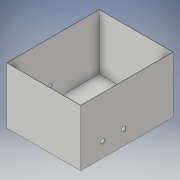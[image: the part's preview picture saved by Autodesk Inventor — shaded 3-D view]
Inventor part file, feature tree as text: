
AUTODESK INVENTOR PART (.ipt)
format: ipt  version: 2018 (Build 220112000, 112)  size: 176,640 bytes
history: native  units: in
note: dims shown in document units (in); Inventor stores cm internally (conversion verified against a paired STEP export)
features: extrude x7, sketch x7
ambient origin geometry x8: Origin, YZ Plane, XZ Plane, XY Plane, X Axis, Y Axis, Z Axis, Center Point
bodies: Solid1 (feature_tree)
feature tree (14):
  extrude  "Extrusion1"  Depth=5.0in
  extrude  "Extrusion2"  Depth=3.96in
  extrude  "Extrusion3"  Depth=3.0in TaperAngle=0.0deg
  extrude  "Extrusion4"  Depth=2.0in
  extrude  "Extrusion5"  Depth=0.164in
  extrude  "Extrusion6"  Depth=1.929in
  extrude  "Extrusion7"  Depth=1.722in
  sketch  "Sketch1"  dims[d0=4.0in d1=5.0in]
  sketch  "Sketch2"  dims[d2=0.04in d3=0.0in d4=3.96in]
  sketch  "Sketch3"  dims[d5=4.96in d6=3.0in d7=0.0in]
  sketch  "Sketch4"  dims[d8=1.0in d9=2.0in]
  sketch  "Sketch5"  dims[d10=0.164in d11=0.164in]
  sketch  "Sketch6"  dims[d12=0.0in d13=0.0in d14=1.929in]
  sketch  "Sketch7"  dims[d15=3.504in d16=1.722in d17=3.504in d18=2.717in d27=0.112in d28=0.112in d29=0.112in d30=0.112in d31=0.0in d32=0.0in d33=0.787in d34=2.598in d35=0.112in d36=0.112in d37=0.112in d38=0.112in d39=0.0in d40=0.0in d41=0.728in d42=0.0in d43=0.438in d44=1.125in d45=180.0deg d46=0.25in d47=0.25in d48=0.0in d49=0.0in d50=0.728in d51=180.0deg d52=0.438in d53=1.125in d54=180.0deg d55=0.25in d56=0.25in d57=0.0in d58=0.0in]
